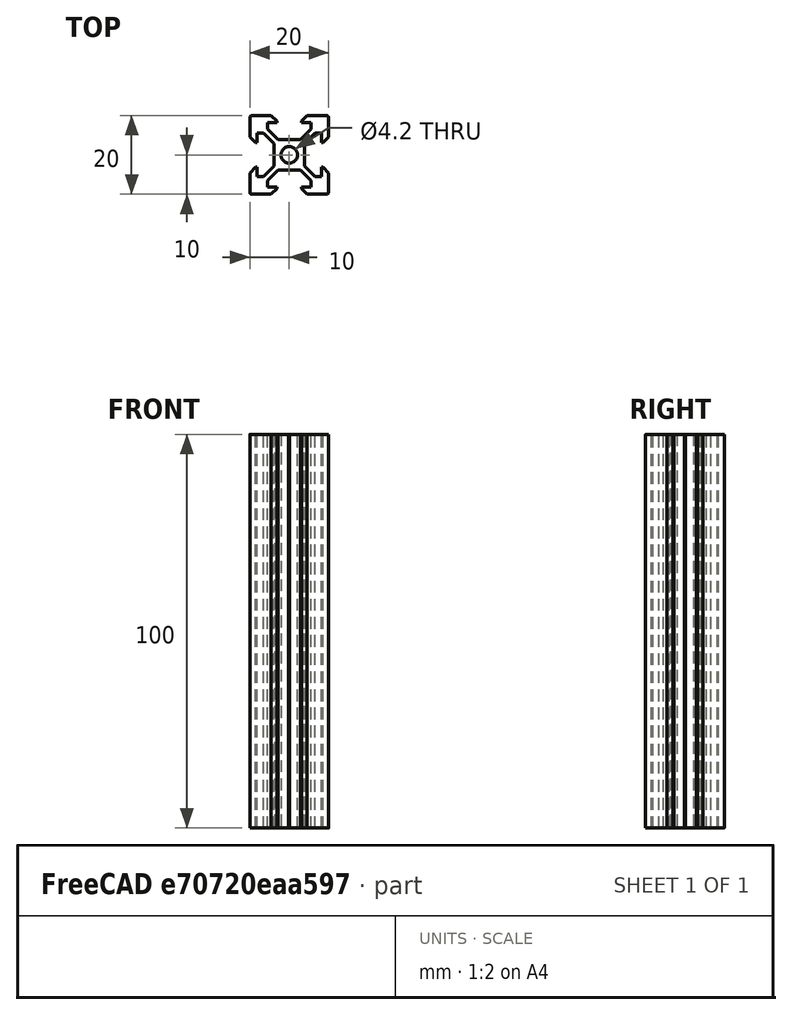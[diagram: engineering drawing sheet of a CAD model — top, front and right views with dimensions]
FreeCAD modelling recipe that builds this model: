
FCSTD DOCUMENT  (FreeCAD 0.20R27861 (Git))
Label: 2020-100
License: All rights reserved
LicenseURL: http://en.wikipedia.org/wiki/All_rights_reserved
objects: Sketcher::SketchObject×1, PartDesign::Pad×1, PartDesign::Body×1
note: 4 computed .brp shape members not serialized (recipe doc carries the construction recipe); baked Part::Feature solids carry a one-line shape summary decoded from their .brp

FEATURE [Sketcher::SketchObject] Sketch
  FullyConstrained = true
  MapMode = 5
  Support = -> [XY_Plane]
  sketch-geometry (65):
    g0: LineSegment StartX=-10 StartY=4.58 StartZ=0 EndX=-10 EndY=9.5 EndZ=0
    g1: LineSegment StartX=-9.5 StartY=10 StartZ=0 EndX=-4.58 EndY=10 EndZ=0
    g2: LineSegment StartX=-5.5 StartY=8.2 StartZ=0 EndX=-3.125 EndY=8.2 EndZ=0
    g3: LineSegment StartX=-8.2 StartY=5.5 StartZ=0 EndX=-8.2 EndY=3.125 EndZ=0
    g4: LineSegment StartX=-0.125 StartY=3.9 StartZ=0 EndX=-2.83934 EndY=3.9 EndZ=0
    g5: LineSegment StartX=-3.9 StartY=2.83934 StartZ=0 EndX=-3.9 EndY=0.125 EndZ=0
    g6: ArcOfCircle CenterX=0 CenterY=3.9 CenterZ=0 NormalX=0 NormalY=0 NormalZ=1 AngleXU=0 Radius=0.125 StartAngle=3.14159 EndAngle=6.28319
    g7: ArcOfCircle CenterX=-3.9 CenterY=0 CenterZ=0 NormalX=0 NormalY=0 NormalZ=1 AngleXU=0 Radius=0.125 StartAngle=4.71239 EndAngle=7.85398
    g8: ArcOfCircle CenterX=-9.5 CenterY=9.5 CenterZ=0 NormalX=0 NormalY=0 NormalZ=1 AngleXU=0 Radius=0.5 StartAngle=1.5708 EndAngle=3.14159
    g9: LineSegment StartX=-5.5 StartY=8.2 StartZ=0 EndX=-5.5 EndY=6.56066 EndZ=0
    g10: LineSegment StartX=-8.2 StartY=5.5 StartZ=0 EndX=-6.56066 EndY=5.5 EndZ=0
    g11: LineSegment StartX=-4.58 StartY=10 StartZ=0 EndX=-3.125 EndY=8.545 EndZ=0
    g12: LineSegment StartX=-3.125 StartY=8.545 StartZ=0 EndX=-3.125 EndY=8.2 EndZ=0
    g13: LineSegment StartX=-10 StartY=4.58 StartZ=0 EndX=-8.545 EndY=3.125 EndZ=0
    g14: LineSegment StartX=-8.545 StartY=3.125 StartZ=0 EndX=-8.2 EndY=3.125 EndZ=0
    g15: LineSegment StartX=-5.5 StartY=6.56066 StartZ=0 EndX=-2.83934 EndY=3.9 EndZ=0
    g16: LineSegment StartX=-6.56066 StartY=5.5 StartZ=0 EndX=-3.9 EndY=2.83934 EndZ=0
    g17: Circle CenterX=0 CenterY=0 CenterZ=0 NormalX=0 NormalY=0 NormalZ=1 AngleXU=0 Radius=2.1
    g18: LineSegment StartX=0.125 StartY=3.9 StartZ=0 EndX=2.83934 EndY=3.9 EndZ=0
    g19: LineSegment StartX=2.83934 StartY=3.9 StartZ=0 EndX=5.5 EndY=6.56066 EndZ=0
    g20: LineSegment StartX=5.5 StartY=6.56066 StartZ=0 EndX=5.5 EndY=8.2 EndZ=0
    g21: LineSegment StartX=3.125 StartY=8.2 StartZ=0 EndX=3.125 EndY=8.545 EndZ=0
    g22: LineSegment StartX=5.5 StartY=8.2 StartZ=0 EndX=3.125 EndY=8.2 EndZ=0
    g23: LineSegment StartX=4.58 StartY=10 StartZ=0 EndX=9.5 EndY=10 EndZ=0
    g24: ArcOfCircle CenterX=9.5 CenterY=9.5 CenterZ=0 NormalX=0 NormalY=0 NormalZ=1 AngleXU=0 Radius=0.5 StartAngle=1.9e-15 EndAngle=1.5708
    g25: LineSegment StartX=10 StartY=9.5 StartZ=0 EndX=10 EndY=4.58 EndZ=0
    g26: LineSegment StartX=10 StartY=4.58 StartZ=0 EndX=8.545 EndY=3.125 EndZ=0
    g27: LineSegment StartX=8.545 StartY=3.125 StartZ=0 EndX=8.2 EndY=3.125 EndZ=0
    g28: LineSegment StartX=8.2 StartY=3.125 StartZ=0 EndX=8.2 EndY=5.5 EndZ=0
    g29: LineSegment StartX=8.2 StartY=5.5 StartZ=0 EndX=6.56066 EndY=5.5 EndZ=0
    g30: LineSegment StartX=6.56066 StartY=5.5 StartZ=0 EndX=3.9 EndY=2.83934 EndZ=0
    g31: LineSegment StartX=3.9 StartY=2.83934 StartZ=0 EndX=3.9 EndY=0.125 EndZ=0
    g32: ArcOfCircle CenterX=3.9 CenterY=0 CenterZ=0 NormalX=0 NormalY=0 NormalZ=1 AngleXU=0 Radius=0.125 StartAngle=1.5708 EndAngle=4.71239
    g33: LineSegment StartX=3.9 StartY=-0.125 StartZ=0 EndX=3.9 EndY=-2.83934 EndZ=0
    g34: LineSegment StartX=3.9 StartY=-2.83934 StartZ=0 EndX=6.56066 EndY=-5.5 EndZ=0
    g35: LineSegment StartX=6.56066 StartY=-5.5 StartZ=0 EndX=8.2 EndY=-5.5 EndZ=0
    g36: LineSegment StartX=8.2 StartY=-5.5 StartZ=0 EndX=8.2 EndY=-3.125 EndZ=0
    g37: LineSegment StartX=8.2 StartY=-3.125 StartZ=0 EndX=8.545 EndY=-3.125 EndZ=0
    g38: LineSegment StartX=8.545 StartY=-3.125 StartZ=0 EndX=10 EndY=-4.58 EndZ=0
    g39: LineSegment StartX=10 StartY=-4.58 StartZ=0 EndX=10 EndY=-9.5 EndZ=0
    g40: ArcOfCircle CenterX=9.5 CenterY=-9.5 CenterZ=0 NormalX=0 NormalY=0 NormalZ=1 AngleXU=0 Radius=0.5 StartAngle=4.71239 EndAngle=6.28319
    g41: LineSegment StartX=9.5 StartY=-10 StartZ=0 EndX=4.58 EndY=-10 EndZ=0
    g42: LineSegment StartX=4.58 StartY=-10 StartZ=0 EndX=3.125 EndY=-8.545 EndZ=0
    g43: LineSegment StartX=2.83934 StartY=-3.9 StartZ=0 EndX=5.5 EndY=-6.56066 EndZ=0
    g44: LineSegment StartX=3.125 StartY=-8.545 StartZ=0 EndX=3.125 EndY=-8.2 EndZ=0
    g45: LineSegment StartX=3.125 StartY=-8.2 StartZ=0 EndX=5.5 EndY=-8.2 EndZ=0
    g46: LineSegment StartX=5.5 StartY=-8.2 StartZ=0 EndX=5.5 EndY=-6.56066 EndZ=0
    g47: ArcOfCircle CenterX=0 CenterY=-3.9 CenterZ=0 NormalX=0 NormalY=0 NormalZ=1 AngleXU=0 Radius=0.125 StartAngle=0 EndAngle=3.14159
    g48: LineSegment StartX=0.125 StartY=-3.9 StartZ=0 EndX=2.83934 EndY=-3.9 EndZ=0
    g49: LineSegment StartX=-0.125 StartY=-3.9 StartZ=0 EndX=-2.83934 EndY=-3.9 EndZ=0
    g50: LineSegment StartX=-3.9 StartY=-0.125 StartZ=0 EndX=-3.9 EndY=-2.83934 EndZ=0
    g51: LineSegment StartX=-3.9 StartY=-2.83934 StartZ=0 EndX=-6.56066 EndY=-5.5 EndZ=0
    g52: LineSegment StartX=-6.56066 StartY=-5.5 StartZ=0 EndX=-8.2 EndY=-5.5 EndZ=0
    g53: LineSegment StartX=-8.2 StartY=-5.5 StartZ=0 EndX=-8.2 EndY=-3.125 EndZ=0
    g54: LineSegment StartX=-8.2 StartY=-3.125 StartZ=0 EndX=-8.545 EndY=-3.125 EndZ=0
    g55: LineSegment StartX=-8.545 StartY=-3.125 StartZ=0 EndX=-10 EndY=-4.58 EndZ=0
    g56: LineSegment StartX=-10 StartY=-4.58 StartZ=0 EndX=-10 EndY=-9.5 EndZ=0
    g57: ArcOfCircle CenterX=-9.5 CenterY=-9.5 CenterZ=0 NormalX=0 NormalY=0 NormalZ=1 AngleXU=0 Radius=0.5 StartAngle=3.14159 EndAngle=4.71239
    g58: LineSegment StartX=-9.5 StartY=-10 StartZ=0 EndX=-4.58 EndY=-10 EndZ=0
    g59: LineSegment StartX=-4.58 StartY=-10 StartZ=0 EndX=-3.125 EndY=-8.545 EndZ=0
    g60: LineSegment StartX=-2.83934 StartY=-3.9 StartZ=0 EndX=-5.5 EndY=-6.56066 EndZ=0
    g61: LineSegment StartX=-5.5 StartY=-6.56066 StartZ=0 EndX=-5.5 EndY=-8.2 EndZ=0
    g62: LineSegment StartX=-5.5 StartY=-8.2 StartZ=0 EndX=-3.125 EndY=-8.2 EndZ=0
    g63: LineSegment StartX=-3.125 StartY=-8.545 StartZ=0 EndX=-3.125 EndY=-8.2 EndZ=0
    g64: LineSegment StartX=3.125 StartY=8.545 StartZ=0 EndX=4.58 EndY=10 EndZ=0
  constraints (194):
    c: Diameter(g17) = 4.2
    c: Radius(g32) = 0.125
    c: Coincident(g-1,g17)
    c: DistanceY(g57,g1) = 20
    c: DistanceX(g56,g39) = 20
    c: Radius(g57) = 0.5
    c: DistanceX(g56,g17) = 10
    c: DistanceY(g57,g17) = 10
    c: Distance(g5,g4) = 1.5
    c: DistanceY(g20,g23) = 1.8
    c: DistanceY(g18,g20) = 4.3
    c: DistanceX(g11,g21) = 6.25
    c: DistanceX(g1,g23) = 9.16
    c: DistanceX(g2,g20) = 11
    c: Coincident(g6,g18)
    c: Coincident(g6,g4)
    c: Coincident(g4,g15)
    c: Coincident(g18,g19)
    c: Coincident(g5,g16)
    c: Coincident(g16,g10)
    c: Coincident(g15,g9)
    c: Coincident(g12,g2)
    c: Coincident(g2,g9)
    c: Coincident(g12,g11)
    c: Coincident(g1,g11)
    c: Coincident(g23,g64)
    c: Coincident(g22,g21)
    c: Coincident(g64,g21)
    c: Coincident(g22,g20)
    c: Coincident(g19,g20)
    c: Coincident(g25,g26)
    c: Coincident(g27,g26)
    c: Coincident(g27,g28)
    c: Coincident(g28,g29)
    c: Coincident(g29,g30)
    c: Coincident(g0,g13)
    c: Coincident(g14,g13)
    c: Coincident(g14,g3)
    c: Coincident(g3,g10)
    c: Coincident(g5,g7)
    c: Coincident(g50,g7)
    c: Coincident(g51,g50)
    c: Coincident(g52,g51)
    c: Coincident(g52,g53)
    c: Coincident(g54,g53)
    c: Coincident(g55,g54)
    c: Coincident(g56,g55)
    c: Coincident(g58,g59)
    c: Coincident(g63,g59)
    c: Coincident(g62,g63)
    c: Coincident(g62,g61)
    c: Coincident(g60,g61)
    c: Coincident(g49,g60)
    c: Coincident(g47,g49)
    c: Coincident(g48,g47)
    c: Coincident(g48,g43)
    c: Coincident(g46,g43)
    c: Coincident(g45,g46)
    c: Coincident(g45,g44)
    c: Coincident(g42,g44)
    c: Coincident(g41,g42)
    c: Coincident(g39,g38)
    c: Coincident(g38,g37)
    c: Coincident(g37,g36)
    c: Coincident(g35,g36)
    c: Coincident(g34,g35)
    c: Coincident(g34,g33)
    c: Coincident(g31,g30)
    c: Coincident(g33,g32)
    c: Coincident(g32,g31)
    c: Vertical(g0)
    c: Horizontal(g1)
    c: Equal(g0,g1)
    c: Horizontal(g4)
    c: PointOnObject(g6,g-2)
    c: Horizontal(g18)
    c: Horizontal(g4,g6)
    c: Horizontal(g6,g6)
    c: Parallel(g13,g11)
    c: Horizontal(g14)
    c: Vertical(g12)
    c: Equal(g14,g12)
    c: Vertical(g3)
    c: Horizontal(g2)
    c: Equal(g3,g2)
    c: Equal(g10,g9)
    c: Horizontal(g10)
    c: Vertical(g9)
    c: Parallel(g16,g15)
    c: Equal(g13,g11)
    c: Tangent(g8,g0) = 1.5708
    c: PointOnObject(g7,g-1)
    c: Vertical(g5)
    c: Vertical(g50)
    c: Vertical(g7,g7)
    c: Vertical(g7,g5)
    c: Horizontal(g52)
    c: Vertical(g53)
    c: Horizontal(g54)
    c: Vertical(g56)
    c: Equal(g50,g5)
    c: Equal(g51,g16)
    c: Perpendicular(g16,g51)
    c: Equal(g52,g10)
    c: Equal(g53,g3)
    c: Equal(g54,g14)
    c: Equal(g55,g13)
    c: Perpendicular(g55,g13)
    c: Equal(g56,g0)
    c: Tangent(g57,g56) = -1.5708
    c: Tangent(g57,g58) = -1.5708
    c: Tangent(g8,g1) = 1.5708
    c: Equal(g57,g8)
    c: Horizontal(g58)
    c: Equal(g58,g56)
    c: Equal(g55,g59)
    c: Parallel(g55,g59)
    c: Vertical(g63)
    c: Equal(g63,g54)
    c: Horizontal(g62)
    c: Vertical(g61)
    c: Equal(g61,g52)
    c: Equal(g60,g51)
    c: Parallel(g60,g51)
    c: PointOnObject(g47,g-2)
    c: Horizontal(g47,g47)
    c: Horizontal(g47,g47)
    c: Horizontal(g49)
    c: Equal(g49,g50)
    c: Horizontal(g48)
    c: Vertical(g46)
    c: Perpendicular(g60,g43)
    c: Equal(g43,g60)
    c: Equal(g46,g61)
    c: Horizontal(g45)
    c: Equal(g45,g62)
    c: Vertical(g44)
    c: Equal(g44,g63)
    c: Perpendicular(g42,g59)
    c: Equal(g42,g59)
    c: Horizontal(g41)
    c: Equal(g58,g41)
    c: Tangent(g40,g41) = 1.5708
    c: Tangent(g40,g39) = 1.5708
    c: Equal(g57,g40)
    c: Vertical(g39)
    c: Equal(g41,g39)
    c: Parallel(g42,g38)
    c: Equal(g42,g38)
    c: Horizontal(g37)
    c: Equal(g44,g37)
    c: Vertical(g36)
    c: Equal(g45,g36)
    c: Horizontal(g35)
    c: Equal(g35,g46)
    c: Parallel(g43,g34)
    c: Equal(g43,g34)
    c: PointOnObject(g32,g-1)
    c: Vertical(g33)
    c: Vertical(g32,g31)
    c: Vertical(g31,g32)
    c: Equal(g48,g33)
    c: Equal(g47,g7)
    c: Equal(g7,g6)
    c: Vertical(g31)
    c: Equal(g33,g31)
    c: Equal(g4,g5)
    c: Equal(g4,g18)
    c: Parallel(g30,g19)
    c: Equal(g30,g19)
    c: Horizontal(g29)
    c: Vertical(g20)
    c: Equal(g35,g29)
    c: Equal(g29,g20)
    c: Horizontal(g22)
    c: Equal(g22,g2)
    c: Vertical(g21)
    c: Equal(g11,g64)
    c: Horizontal(g23)
    c: Equal(g1,g23)
    c: Vertical(g28)
    c: Equal(g28,g36)
    c: Horizontal(g27)
    c: Equal(g27,g37)
    c: Perpendicular(g38,g26)
    c: Equal(g38,g26)
    c: Vertical(g25)
    c: Equal(g39,g25)
    c: Tangent(g24,g23) = 1.5708
    c: Tangent(g24,g25) = 1.5708
    c: Vertical(g25,g38)
    c: Horizontal(g2,g21)
    c: Vertical(g10,g51)
    c: Angle(g64,g11) = 1.5708
FEATURE [PartDesign::Pad] Pad
  Direction = (0,0,1)
  Length = 100
  Length2 = 100
  Profile = -> Sketch
  ReferenceAxis = -> Sketch [N_Axis]
  Type = 0
FEATURE [PartDesign::Body] Body  label="2020-100"
  Group = -> [Sketch,Pad]
  Origin = -> Origin
  Tip = -> Pad
